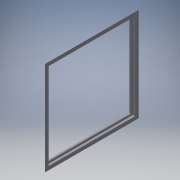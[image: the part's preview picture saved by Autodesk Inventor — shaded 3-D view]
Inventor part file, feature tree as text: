
AUTODESK INVENTOR PART (.ipt)
format: ipt  version: 2018.3 (Build 223284000, 284)  size: 156,672 bytes
history: native  units: mm
features: reference x21, extrude x4, sketch x4, projected_geometry x3, other x3, chamfer x2
ambient origin geometry x8: Origin, YZ Plane, XZ Plane, XY Plane, X Axis, Y Axis, Z Axis, Center Point
bodies: Volumenkörper1 (feature_tree)
feature tree (37):
  extrude  "Extrusion1"  Depth=440.0mm
  extrude  "Extrusion2"  Depth=17.0mm
  extrude  "Extrusion3"  Depth=17.0mm
  extrude  "Extrusion4"  Depth=10.0mm TaperAngle=0.0deg
  chamfer  "Fase1"  Distance=10.0mm
  chamfer  "Fase2"  Distance=10.0mm
  sketch  "Skizze1"  dims[d0=440.0mm d1=440.0mm]
  sketch  "Skizze2"  dims[d2=18.0mm d3=0.0mm d4=17.0mm]
  projected_geometry  "Projizierte Kontur1"
  sketch  "Skizze3"  dims[d5=17.0mm d6=17.0mm]
  projected_geometry  "Projizierte Kontur2"
  sketch  "Skizze6"  dims[d7=17.0mm d8=10.0mm d9=0.0mm d10=10.0mm d11=10.0mm d12=10.0mm d13=10.0mm d14=8.0mm d15=0.0mm d24=15.0mm d25=0.0mm d26=18.0mm d27=2.0mm d28=45.0deg d31=18.0mm d32=2.0mm d33=45.0deg]
  projected_geometry  "Projizierte Kontur4"
  reference  "Referenz29"
  reference  "Referenz30"
  reference  "Referenz31"
  reference  "Referenz32"
  reference  "Referenz33"
  reference  "Referenz34"
  reference  "Referenz35"
  reference  "Referenz36"
  reference  "Referenz37"
  reference  "Referenz38"
  reference  "Referenz39"
  reference  "Referenz40"
  reference  "Referenz41"
  reference  "Referenz42"
  reference  "Referenz43"
  reference  "Referenz44"
  reference  "Referenz45"
  reference  "Referenz46"
  reference  "Referenz47"
  reference  "Referenz48"
  reference  "Referenz49"
  parser-record x1  (decoder bookkeeping rows leaked as tree rows — omitted from the tree; the rows remain in map.json)
  other  "Baugruppe1.iam"
  other  "PV_Modul_CPY_3:1"
note: 1 file-system path scrubbed to <path> (originals preserved in map.json)
